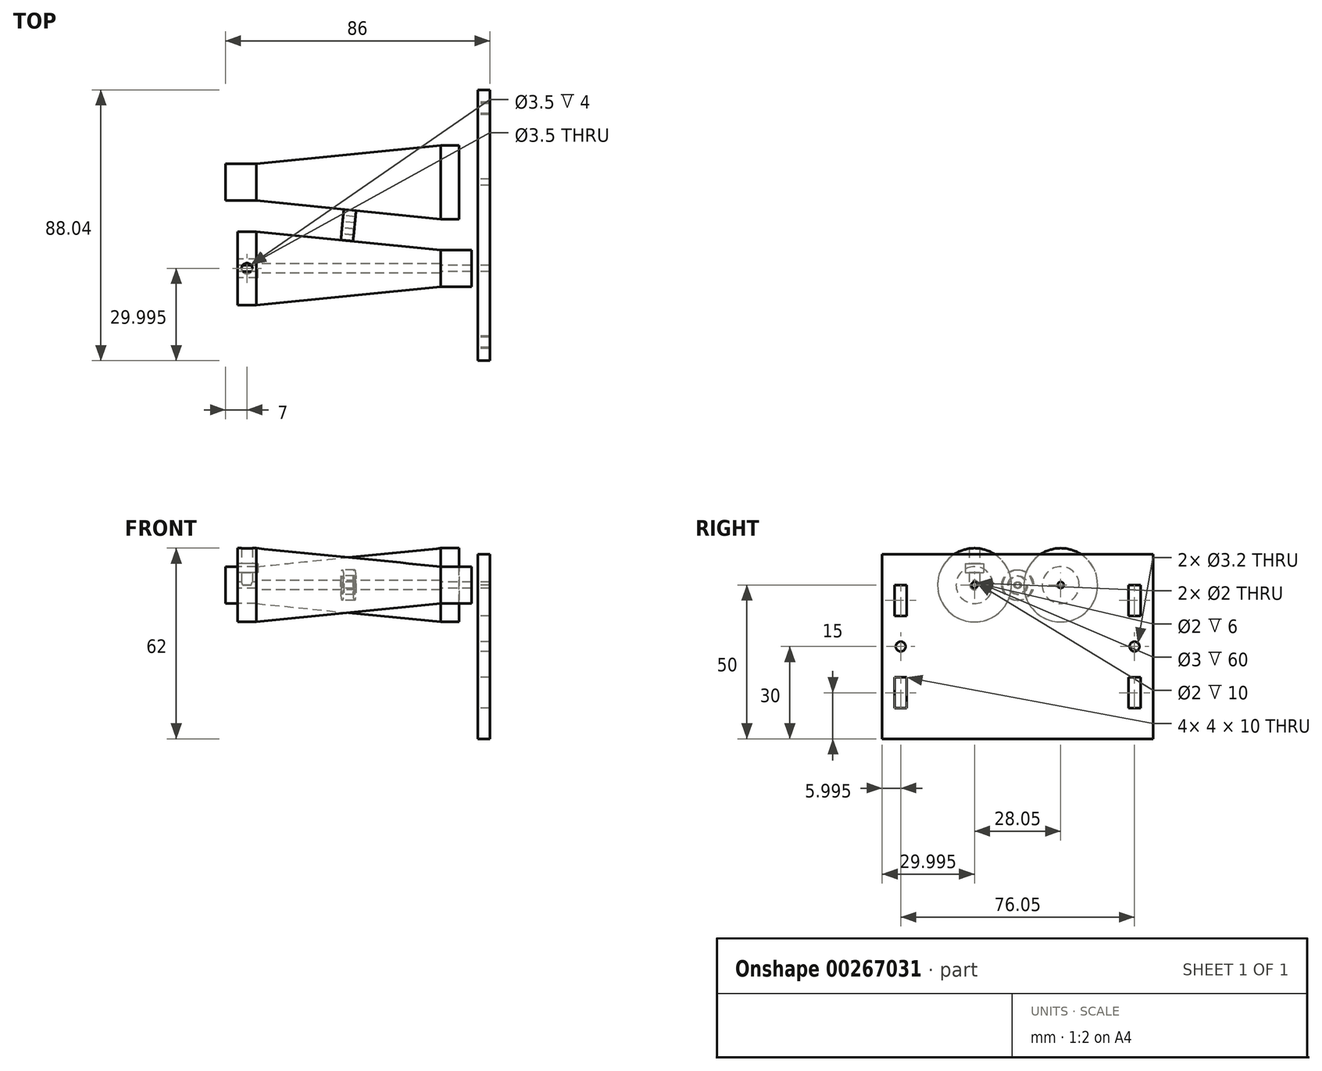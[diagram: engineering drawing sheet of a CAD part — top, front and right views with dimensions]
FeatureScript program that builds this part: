
annotation { "Feature Type Name" : "Feature", "Feature Type Description" : "" }
export const myFeature = defineFeature(function(context is Context, id is Id, definition is map)
    precondition{}
    {
        {
            assignVariable(context, id + "F0", {"name" : "cone_hub_l_2", "anyValue" : 6});
        }
        {
            assignVariable(context, id + "F1", {"name" : "cone_captured_nut_l", "anyValue" : 7});
        }
        {
            var Q0;
            Q0=qCreatedBy(makeId("Top.planeOp"),FACE);
            var sketch = newSketch(context, id + "F2", { "sketchPlane" : qUnion([Q0])});
            skLineSegment(sketch, "E0.bottom", {"start": v(42, 36.02) * mm, "end": v(-42, 36.02) * mm, "construction": true});
            skLineSegment(sketch, "E0.top", {"start": v(42, -36.02) * mm, "end": v(-42, -36.02) * mm, "construction": true});
            skLineSegment(sketch, "E0.left", {"start": v(42, 36.02) * mm, "end": v(42, -36.02) * mm, "construction": true});
            skLineSegment(sketch, "E0.right", {"start": v(-42, 36.02) * mm, "end": v(-42, -36.02) * mm, "construction": true});
            skPoint(sketch, "E0.middle", {"position": v(0, 0) * mm});
            skLineSegment(sketch, "E1", {"start": v(-42, 4.2) * mm, "end": v(42, -4.2) * mm, "construction": true});
            skLineSegment(sketch, "E2", {"start": v(-42, 5.2) * mm, "end": v(42, -3.2) * mm, "construction": true});
            skLineSegment(sketch, "E3", {"start": v(42, -5.2) * mm, "end": v(-42, 3.2) * mm, "construction": true});
            skLineSegment(sketch, "E4", {"start": v(-1.5, 5.17) * mm, "end": v(2.49, 4.78) * mm, "construction": true});
            skLineSegment(sketch, "E5", {"start": v(2.49, 4.78) * mm, "end": v(1.5, -5.17) * mm, "construction": true});
            skLineSegment(sketch, "E6", {"start": v(1.5, -5.17) * mm, "end": v(-2.49, -4.78) * mm, "construction": true});
            skLineSegment(sketch, "E7", {"start": v(-2.49, -4.78) * mm, "end": v(-1.5, 5.17) * mm, "construction": true});
            skLineSegment(sketch, "E8", {"start": v(-0.5, -4.98) * mm, "end": v(0.5, 4.98) * mm, "construction": true});
            skLineSegment(sketch, "E9", {"start": v(-42, 14.02) * mm, "end": v(42, 14.02) * mm, "construction": true});
            skLineSegment(sketch, "E10", {"start": v(-42, -14.02) * mm, "end": v(42, -14.02) * mm, "construction": true});
            skLineSegment(sketch, "E11", {"start": v(-30, -2.02) * mm, "end": v(-30, -26.02) * mm, "construction": true});
            skLineSegment(sketch, "E12", {"start": v(-30, -26.02) * mm, "end": v(30, -20.02) * mm, "construction": true});
            skLineSegment(sketch, "E13", {"start": v(30, -20.02) * mm, "end": v(30, -8.02) * mm, "construction": true});
            skLineSegment(sketch, "E14", {"start": v(30, -8.02) * mm, "end": v(-30, -2.02) * mm, "construction": true});
            skPoint(sketch, "E15", {"position": v(-30, -14.02) * mm});
            skPoint(sketch, "E16", {"position": v(30, -14.02) * mm});
            skLineSegment(sketch, "E17", {"start": v(30, -8.02) * mm, "end": v(40, -8.02) * mm, "construction": true});
            skLineSegment(sketch, "E18", {"start": v(40, -8.02) * mm, "end": v(40, -20.02) * mm, "construction": true});
            skLineSegment(sketch, "E19", {"start": v(40, -20.02) * mm, "end": v(30, -20.02) * mm, "construction": true});
            skLineSegment(sketch, "E20", {"start": v(-30, -2.02) * mm, "end": v(-36, -2.02) * mm, "construction": true});
            skLineSegment(sketch, "E21", {"start": v(-36, -2.02) * mm, "end": v(-36, -26.02) * mm, "construction": true});
            skLineSegment(sketch, "E22", {"start": v(-36, -26.02) * mm, "end": v(-30, -26.02) * mm, "construction": true});
            skLineSegment(sketch, "E23", {"start": v(-30, 20.02) * mm, "end": v(-40, 20.02) * mm, "construction": true});
            skLineSegment(sketch, "E24", {"start": v(-40, 20.02) * mm, "end": v(-40, 8.02) * mm, "construction": true});
            skLineSegment(sketch, "E25", {"start": v(-40, 8.02) * mm, "end": v(-30, 8.02) * mm, "construction": true});
            skLineSegment(sketch, "E26", {"start": v(-30, 8.02) * mm, "end": v(-30, 20.02) * mm, "construction": true});
            skLineSegment(sketch, "E27", {"start": v(-30, 20.02) * mm, "end": v(30, 26.02) * mm, "construction": true});
            skLineSegment(sketch, "E28", {"start": v(30, 26.02) * mm, "end": v(30, 2.02) * mm, "construction": true});
            skLineSegment(sketch, "E29", {"start": v(30, 2.02) * mm, "end": v(36, 2.02) * mm, "construction": true});
            skLineSegment(sketch, "E30", {"start": v(36, 2.02) * mm, "end": v(36, 26.02) * mm, "construction": true});
            skLineSegment(sketch, "E31", {"start": v(36, 26.02) * mm, "end": v(30, 26.02) * mm, "construction": true});
            skLineSegment(sketch, "E32", {"start": v(30, 2.02) * mm, "end": v(-30, 8.02) * mm, "construction": true});
            skPoint(sketch, "E33", {"position": v(36, 14.02) * mm});
            skPoint(sketch, "E34", {"position": v(-40, 14.02) * mm});
            skLineSegment(sketch, "E35", {"start": v(-42, 40.02) * mm, "end": v(42, 40.02) * mm, "construction": true});
            skLineSegment(sketch, "E36", {"start": v(42, 40.02) * mm, "end": v(42, 44.02) * mm, "construction": true});
            skLineSegment(sketch, "E37", {"start": v(42, 44.02) * mm, "end": v(46, 44.02) * mm, "construction": true});
            skLineSegment(sketch, "E38", {"start": v(46, 44.02) * mm, "end": v(46, -44.02) * mm, "construction": true});
            skLineSegment(sketch, "E39", {"start": v(46, -44.02) * mm, "end": v(42, -44.02) * mm, "construction": true});
            skLineSegment(sketch, "E40", {"start": v(42, -44.02) * mm, "end": v(42, -40.02) * mm, "construction": true});
            skLineSegment(sketch, "E41", {"start": v(42, -40.02) * mm, "end": v(-42, -40.02) * mm, "construction": true});
            skLineSegment(sketch, "E42", {"start": v(-42, -40.02) * mm, "end": v(-42, -44.02) * mm, "construction": true});
            skLineSegment(sketch, "E43", {"start": v(-42, -44.02) * mm, "end": v(-46, -44.02) * mm, "construction": true});
            skLineSegment(sketch, "E44", {"start": v(-46, -44.02) * mm, "end": v(-46, 44.02) * mm, "construction": true});
            skLineSegment(sketch, "E45", {"start": v(-46, 44.02) * mm, "end": v(-42, 44.02) * mm, "construction": true});
            skLineSegment(sketch, "E46", {"start": v(-42, 44.02) * mm, "end": v(-42, 40.02) * mm, "construction": true});
            skLineSegment(sketch, "E47", {"start": v(42, -4.2) * mm, "end": v(46, -4.6) * mm, "construction": true});
            skLineSegment(sketch, "E48", {"start": v(-42, 4.2) * mm, "end": v(-46, 4.6) * mm, "construction": true});
            skLineSegment(sketch, "E49", {"start": v(40, -13.02) * mm, "end": v(30, -13.02) * mm, "construction": true});
            skLineSegment(sketch, "E50", {"start": v(30, -12.52) * mm, "end": v(-30, -12.52) * mm, "construction": true});
            skLineSegment(sketch, "E51", {"start": v(-30, -13.02) * mm, "end": v(-36, -13.02) * mm, "construction": true});
            skLineSegment(sketch, "E52", {"start": v(-36, -15.02) * mm, "end": v(-30, -15.02) * mm, "construction": true});
            skLineSegment(sketch, "E53", {"start": v(-30, -15.52) * mm, "end": v(30, -15.52) * mm, "construction": true});
            skLineSegment(sketch, "E54", {"start": v(30, -15.02) * mm, "end": v(40, -15.02) * mm, "construction": true});
            skLineSegment(sketch, "E55", {"start": v(2.29, 2.79) * mm, "end": v(-1.7, 3.18) * mm, "construction": true});
            skLineSegment(sketch, "E56", {"start": v(-2.29, -2.79) * mm, "end": v(1.7, -3.18) * mm, "construction": true});
            skSolve(sketch);
        }
        {
            var Q0;
            Q0=qCreatedBy(makeId("Top.planeOp"),FACE);
            var sketch = newSketch(context, id + "F3", { "sketchPlane" : qUnion([Q0])});
            skLineSegment(sketch, "E57", {"start": v(-36, -13.02) * mm, "end": v(-30, -13.02) * mm});
            skLineSegment(sketch, "E58", {"start": v(-30, -13.02) * mm, "end": v(-30, -12.52) * mm});
            skLineSegment(sketch, "E59", {"start": v(-30, -12.52) * mm, "end": v(30, -12.52) * mm});
            skLineSegment(sketch, "E60", {"start": v(30, -12.52) * mm, "end": v(30, -13.02) * mm});
            skLineSegment(sketch, "E61", {"start": v(30, -13.02) * mm, "end": v(40, -13.02) * mm});
            skLineSegment(sketch, "E62", {"start": v(40, -13.02) * mm, "end": v(40, -8.02) * mm});
            skLineSegment(sketch, "E63", {"start": v(40, -8.02) * mm, "end": v(30, -8.02) * mm});
            skLineSegment(sketch, "E64", {"start": v(30, -8.02) * mm, "end": v(-30, -2.02) * mm});
            skLineSegment(sketch, "E65", {"start": v(-30, -2.02) * mm, "end": v(-36, -2.02) * mm});
            skLineSegment(sketch, "E66", {"start": v(-36, -2.02) * mm, "end": v(-36, -13.02) * mm});
            skSolve(sketch);
        }
        {
            var Q0;
            Q0 = qSketchRegion(id + "F3", true);
            var Q1;
            Q1=sQuery(id+"F2.wireOp",EDGE,"E10");
            revolve(context, id + "F4", {"entities" : qUnion([Q0]), "axis" : qUnion([Q1]), "revolveType" : RevolveType.FULL});
        }
        {
            var Q0;
            Q0=qCreatedBy(makeId("Top.planeOp"),FACE);
            var sketch = newSketch(context, id + "F5", { "sketchPlane" : qUnion([Q0])});
            skLineSegment(sketch, "E67", {"start": v(36, 26.02) * mm, "end": v(30, 26.02) * mm});
            skLineSegment(sketch, "E68", {"start": v(30, 26.02) * mm, "end": v(-30, 20.02) * mm});
            skLineSegment(sketch, "E69", {"start": v(-30, 20.02) * mm, "end": v(-40, 20.02) * mm});
            skLineSegment(sketch, "E70", {"start": v(-40, 20.02) * mm, "end": v(-40, 14.02) * mm});
            skLineSegment(sketch, "E71", {"start": v(-40, 14.02) * mm, "end": v(36, 14.02) * mm});
            skLineSegment(sketch, "E72", {"start": v(36, 14.02) * mm, "end": v(36, 26.02) * mm});
            skSolve(sketch);
        }
        {
            var Q0;
            Q0 = qSketchRegion(id + "F5", true);
            var Q1;
            Q1=sQuery(id+"F2.wireOp",EDGE,"E9");
            revolve(context, id + "F6", {"entities" : qUnion([Q0]), "axis" : qUnion([Q1]), "revolveType" : RevolveType.FULL});
        }
        {
            var Q0;
            Q0=qCreatedBy(makeId("Top.planeOp"),FACE);
            var sketch = newSketch(context, id + "F7", { "sketchPlane" : qUnion([Q0])});
            skLineSegment(sketch, "E73", {"start": v(-1.7, 3.18) * mm, "end": v(2.29, 2.79) * mm});
            skLineSegment(sketch, "E74", {"start": v(2.29, 2.79) * mm, "end": v(2.09, 0.8) * mm});
            skLineSegment(sketch, "E75", {"start": v(2.09, 0.8) * mm, "end": v(-1.9, 1.2) * mm});
            skLineSegment(sketch, "E76", {"start": v(-1.9, 1.2) * mm, "end": v(-1.7, 3.18) * mm});
            skSolve(sketch);
        }
        {
            var Q0;
            Q0 = qSketchRegion(id + "F7", true);
            var Q1;
            Q1=sQuery(id+"F2.wireOp",EDGE,"E1");
            revolve(context, id + "F8", {"entities" : qUnion([Q0]), "axis" : qUnion([Q1]), "revolveType" : RevolveType.FULL});
        }
        {
            var Q0;
            Q0=qCreatedBy(makeId("Top.planeOp"),FACE);
            var sketch = newSketch(context, id + "F9", { "sketchPlane" : qUnion([Q0])});
            skLineSegment(sketch, "E77", {"start": v(-1.7, 3.18) * mm, "end": v(2.29, 2.79) * mm});
            skLineSegment(sketch, "E78", {"start": v(2.29, 2.79) * mm, "end": v(2.49, 4.78) * mm});
            skLineSegment(sketch, "E79", {"start": v(2.49, 4.78) * mm, "end": v(-1.5, 5.17) * mm});
            skLineSegment(sketch, "E80", {"start": v(-1.5, 5.17) * mm, "end": v(-1.7, 3.18) * mm});
            skSolve(sketch);
        }
        {
            var Q0;
            Q0 = qSketchRegion(id + "F9", true);
            var Q1;
            Q1=sQuery(id+"F2.wireOp",EDGE,"E1");
            revolve(context, id + "F10", {"entities" : qUnion([Q0]), "axis" : qUnion([Q1]), "revolveType" : RevolveType.FULL});
        }
        {
            var Q0;
            Q0=qCreatedBy(makeId("Top.planeOp"),FACE);
            var sketch = newSketch(context, id + "F11", { "sketchPlane" : qUnion([Q0])});
            skLineSegment(sketch, "E81", {"start": v(-33, -13.02) * mm, "end": v(-33, -15.02) * mm, "construction": true});
            skPoint(sketch, "E82", {"position": v(-33, -14.02) * mm});
            skCircle(sketch, "E83", {"center": v(-33, -14.02) * mm, "radius": 1.75 * mm});
            skSolve(sketch);
        }
        {
            var Q0;
            Q0 = qSketchRegion(id + "F11", true);
            extrude(context, id + "F12", {"entities" : qUnion([Q0]), "operationType" : NewBodyOperationType.REMOVE, "endBound" : BoundingType.THROUGH_ALL, "depth" : 25 * mm});
        }
        {
            var Q0;
            Q0=makeQuery(id+"F4.opRevolve","SWEPT_FACE",FACE,{"disambiguationData":[OSD([sQuery(id+"F3.wireOp",EDGE,"E66")])]});
            var sketch = newSketch(context, id + "F13", { "sketchPlane" : qUnion([Q0])});
            skLineSegment(sketch, "E84", {"start": v(14.02, 0) * mm, "end": v(14.02, 12) * mm, "construction": true});
            skLineSegment(sketch, "E85.bottom", {"start": v(17.02, 7) * mm, "end": v(11.02, 7) * mm});
            skLineSegment(sketch, "E85.top", {"start": v(17.02, 4) * mm, "end": v(11.02, 4) * mm});
            skLineSegment(sketch, "E85.left", {"start": v(17.02, 7) * mm, "end": v(17.02, 4) * mm});
            skLineSegment(sketch, "E85.right", {"start": v(11.02, 7) * mm, "end": v(11.02, 4) * mm});
            skPoint(sketch, "E85.middle", {"position": v(14.02, 5.5) * mm});
            skSolve(sketch);
        }
        {
            var Q0;
            Q0 = qSketchRegion(id + "F13", true);
            extrude(context, id + "F14", {"entities" : qUnion([Q0]), "operationType" : NewBodyOperationType.REMOVE, "oppositeDirection" : true, "depth" : (getVariable(context, 'cone_hub_l_2') / 2 + getVariable(context, 'cone_captured_nut_l') / 2) * mm});
        }
        {
            var Q0;
            Q0=qCreatedBy(makeId("Right.planeOp"),FACE);
            var Q1;
            Q1=sQuery(id+"F2.wireOp",VERTEX,"E1.end");
            cPlane(context, id + "F15", {"entities" : qUnion([Q0, Q1]), "cplaneType" : CPlaneType.PLANE_POINT, "offset" : 25 * mm, "width" : 150 * mm, "height" : 150 * mm});
        }
        {
            var Q0;
            Q0=qCreatedBy(id+"F15.planeOp",FACE);
            var sketch = newSketch(context, id + "F16", { "sketchPlane" : qUnion([Q0])});
            skLineSegment(sketch, "E86", {"start": v(-44.02, 0) * mm, "end": v(-44.02, 10) * mm});
            skLineSegment(sketch, "E87", {"start": v(-44.02, 10) * mm, "end": v(44.02, 10) * mm});
            skLineSegment(sketch, "E88", {"start": v(44.02, 10) * mm, "end": v(44.02, 0) * mm});
            skLineSegment(sketch, "E89", {"start": v(44.02, 0) * mm, "end": v(44.02, -50) * mm});
            skLineSegment(sketch, "E90", {"start": v(44.02, -50) * mm, "end": v(-44.02, -50) * mm});
            skLineSegment(sketch, "E91", {"start": v(-44.02, -50) * mm, "end": v(-44.02, 0) * mm});
            skCircle(sketch, "E92", {"center": v(-14.02, 0) * mm, "radius": 1 * mm});
            skCircle(sketch, "E93", {"center": v(14.02, 0) * mm, "radius": 1 * mm});
            skLineSegment(sketch, "E94.bottom", {"start": v(-40.02, 0) * mm, "end": v(-36.02, 0) * mm});
            skLineSegment(sketch, "E94.top", {"start": v(-40.02, -10) * mm, "end": v(-36.02, -10) * mm});
            skLineSegment(sketch, "E94.left", {"start": v(-40.02, 0) * mm, "end": v(-40.02, -10) * mm});
            skLineSegment(sketch, "E94.right", {"start": v(-36.02, 0) * mm, "end": v(-36.02, -10) * mm});
            skLineSegment(sketch, "E95.bottom", {"start": v(-40.02, -30) * mm, "end": v(-36.02, -30) * mm});
            skLineSegment(sketch, "E95.top", {"start": v(-40.02, -40) * mm, "end": v(-36.02, -40) * mm});
            skLineSegment(sketch, "E95.left", {"start": v(-40.02, -30) * mm, "end": v(-40.02, -40) * mm});
            skLineSegment(sketch, "E95.right", {"start": v(-36.02, -30) * mm, "end": v(-36.02, -40) * mm});
            skLineSegment(sketch, "E96.bottom", {"start": v(36.02, 0) * mm, "end": v(40.02, 0) * mm});
            skLineSegment(sketch, "E96.top", {"start": v(36.02, -10) * mm, "end": v(40.02, -10) * mm});
            skLineSegment(sketch, "E96.left", {"start": v(36.02, 0) * mm, "end": v(36.02, -10) * mm});
            skLineSegment(sketch, "E96.right", {"start": v(40.02, 0) * mm, "end": v(40.02, -10) * mm});
            skLineSegment(sketch, "E97.bottom", {"start": v(36.02, -30) * mm, "end": v(40.02, -30) * mm});
            skLineSegment(sketch, "E97.top", {"start": v(36.02, -40) * mm, "end": v(40.02, -40) * mm});
            skLineSegment(sketch, "E97.left", {"start": v(36.02, -30) * mm, "end": v(36.02, -40) * mm});
            skLineSegment(sketch, "E97.right", {"start": v(40.02, -30) * mm, "end": v(40.02, -40) * mm});
            skPoint(sketch, "E98", {"position": v(-38.02, 0) * mm});
            skPoint(sketch, "E99", {"position": v(38.02, 0) * mm});
            skLineSegment(sketch, "E100", {"start": v(38.02, 10) * mm, "end": v(38.02, -50) * mm, "construction": true});
            skLineSegment(sketch, "E101", {"start": v(-38.02, 10) * mm, "end": v(-38.02, -50) * mm, "construction": true});
            skPoint(sketch, "E102", {"position": v(38.02, -20) * mm});
            skPoint(sketch, "E103", {"position": v(-38.02, -20) * mm});
            skCircle(sketch, "E104", {"center": v(-38.02, -20) * mm, "radius": 1.6 * mm});
            skCircle(sketch, "E105", {"center": v(38.02, -20) * mm, "radius": 1.6 * mm});
            skSolve(sketch);
        }
        {
            var Q0;
            Q0 = qSketchRegion(id + "F16", true);
            var Q1;
            Q1=sQuery(id+"F2.wireOp",VERTEX,"E47.end");
            extrude(context, id + "F17", {"entities" : qUnion([Q0]), "endBound" : BoundingType.UP_TO_VERTEX, "endBoundEntityVertex" : qUnion([Q1]), "depth" : 25 * mm});
        }
    });
